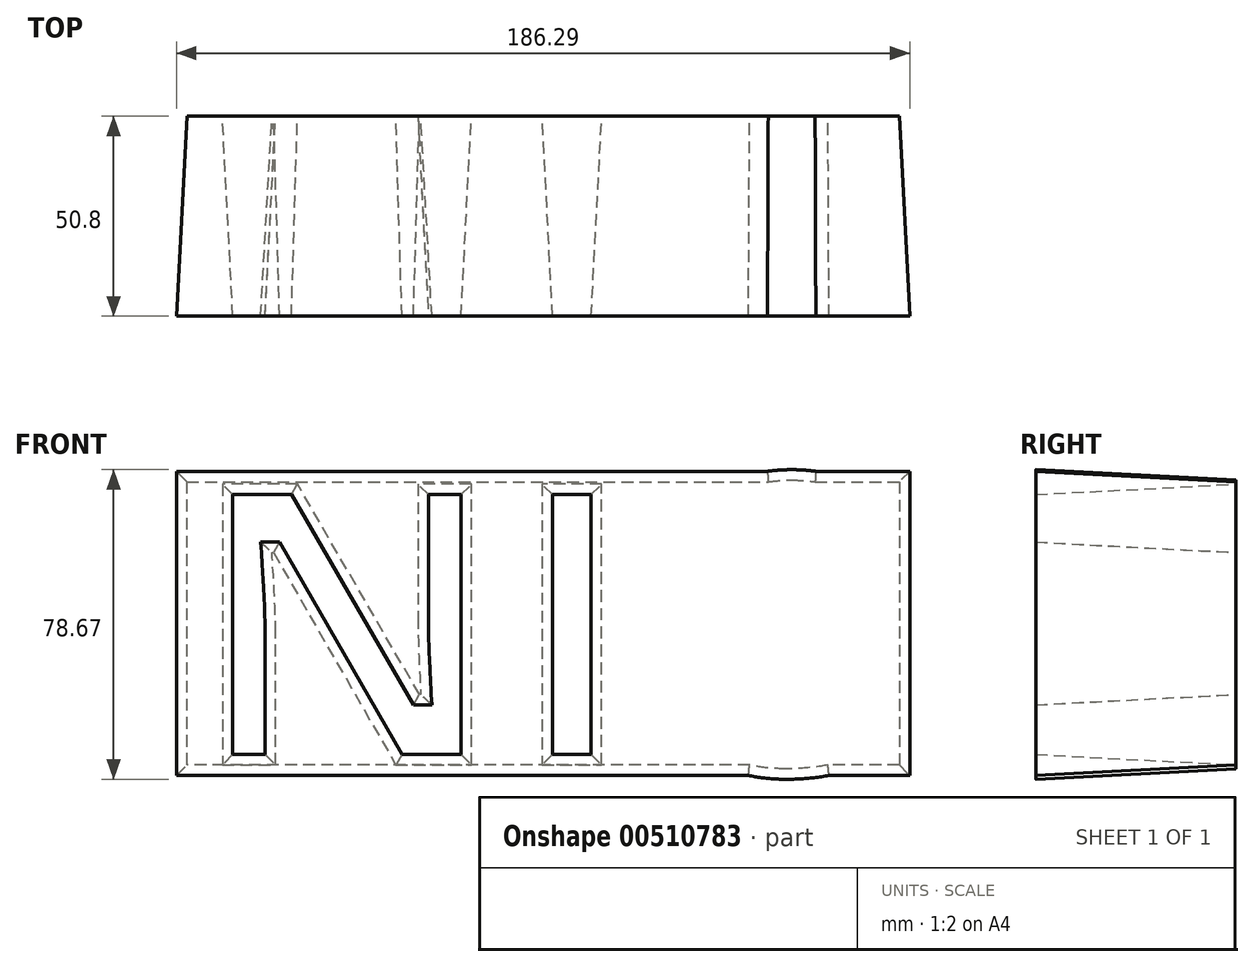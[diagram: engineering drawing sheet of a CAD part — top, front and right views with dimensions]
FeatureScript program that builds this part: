
annotation { "Feature Type Name" : "Feature", "Feature Type Description" : "" }
export const myFeature = defineFeature(function(context is Context, id is Id, definition is map)
    precondition{}
    {
        {
            var Q0;
            Q0=qCreatedBy(makeId("Front.planeOp"),FACE);
            var sketch = newSketch(context, id + "F0", { "sketchPlane" : qUnion([Q0])});
            skLineSegment(sketch, "E0.bottom", {"start": v(-77.47, 29.28) * mm, "end": v(103.5, 29.28) * mm});
            skLineSegment(sketch, "E0.top", {"start": v(-77.47, -42.66) * mm, "end": v(103.5, -42.66) * mm});
            skLineSegment(sketch, "E0.left", {"start": v(-77.47, 29.28) * mm, "end": v(-77.47, -42.66) * mm});
            skLineSegment(sketch, "E0.right", {"start": v(103.5, 29.28) * mm, "end": v(103.5, -42.66) * mm});
            skText(sketch, "E1", { "text": "NIC", "fontName": "OpenSans-Bold.ttf"});
            const initialGuessF0  = {"E1": [-0.07747, -0.04266, 1, 0, 0.07195]};
            skSetInitialGuess(sketch, initialGuessF0);
            skSolve(sketch);
        }
        {
            var Q0;
            Q0 = qSketchRegion(id + "F0", true);
            extrude(context, id + "F1", {"entities" : qUnion([Q0]), "depth" : 50.8 * mm, "hasDraft" : true, "draftAngle" : 3 * degree});
        }
    });
